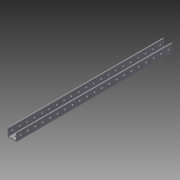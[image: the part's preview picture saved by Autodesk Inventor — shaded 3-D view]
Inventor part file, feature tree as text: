
AUTODESK INVENTOR PART (.ipt)
format: ipt  version: 2014 (Build 180170000, 170)  size: 156,160 bytes
history: native  units: in
note: dims shown in document units (in); Inventor stores cm internally (conversion verified against a paired STEP export)
features: sketch x3, hole x2, extrude x1, pattern_linear x1
ambient origin geometry x8: Origin, YZ Plane, XZ Plane, XY Plane, X Axis, Y Axis, Z Axis, Center Point
bodies: Solid1 (feature_tree)
feature tree (7):
  extrude  "Extrusion1"  Depth=21.0in TaperAngle=0.0deg
  hole  "Hole1"  [1 undecoded]
  hole  "Hole2"  [1 undecoded]
  pattern_linear  "Rectangular Pattern1"  [2 undecoded]
  sketch  "Sketch1"  dims[d0=1.25in d1=1.125in d2=0.0625in d3=0.125in d4=21.0in d5=0.0in]
  sketch  "Sketch2"  dims[d6=0.5in]
  sketch  "Sketch3"  dims[d7=0.25in d8=0.75in d9=0.375in d10=0.25in d11=0.5635in d12=1.0in d13=0.8108in d14=0.5in d15=0.25in d16=0.75in d17=0.375in d18=0.25in d19=0.5635in d20=1.0in d21=0.8108in d22=8.2677in d24=1.0in]
note: 4 required parameter values undecoded (feature->parameter linkage not recoverable at this tier; creation-order binding heuristic only, values carry confidence <= 0.55)
